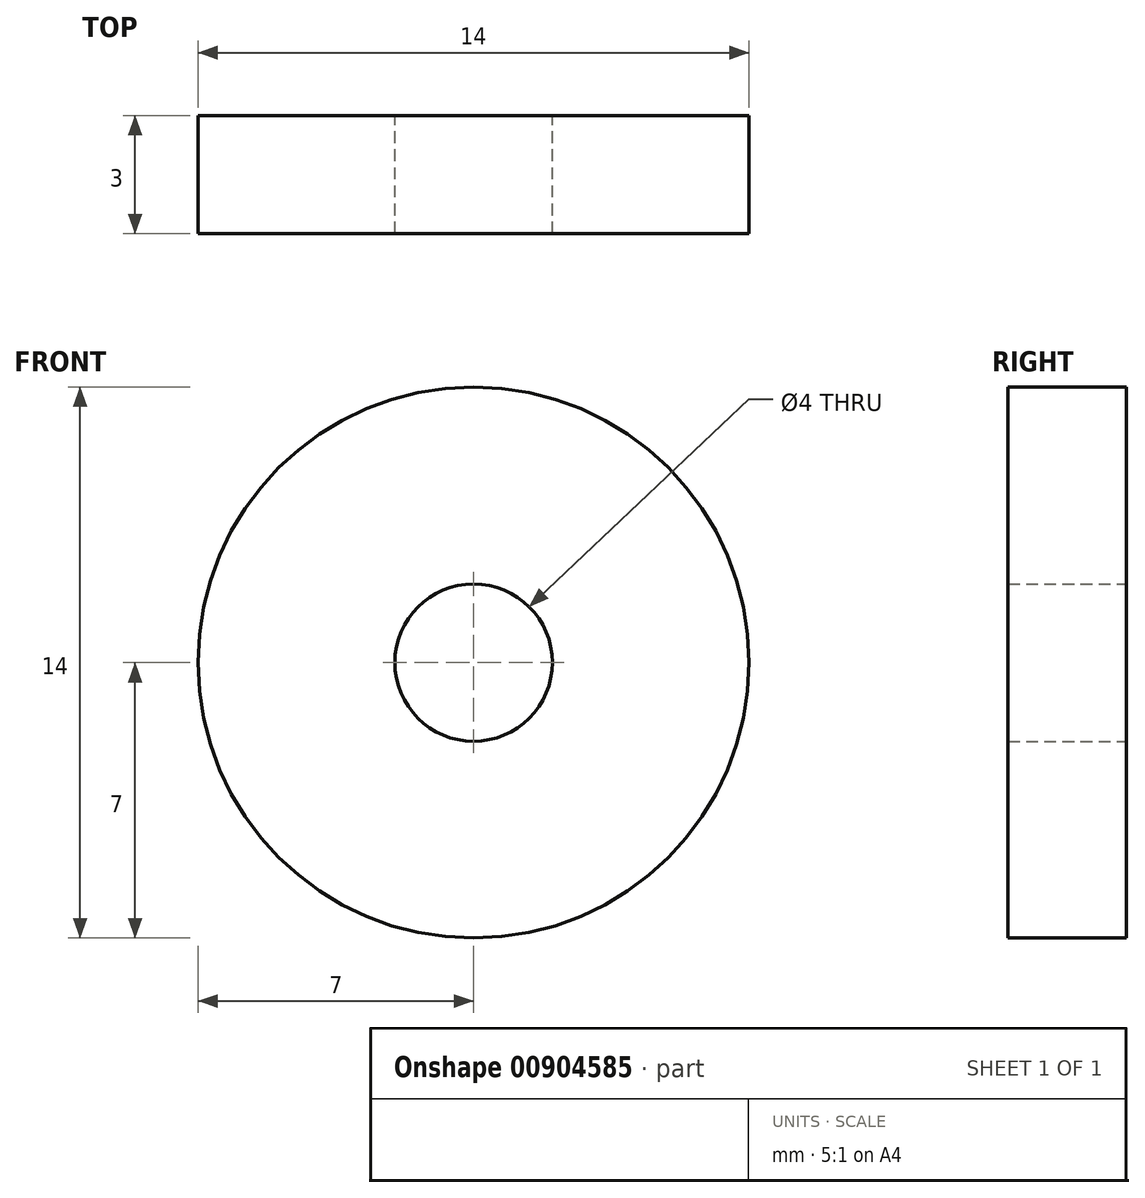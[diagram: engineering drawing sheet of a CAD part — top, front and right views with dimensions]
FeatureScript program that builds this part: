
annotation { "Feature Type Name" : "Feature", "Feature Type Description" : "" }
export const myFeature = defineFeature(function(context is Context, id is Id, definition is map)
    precondition{}
    {
        {
            var Q0;
            Q0=qCreatedBy(makeId("Front.planeOp"),FACE);
            var sketch = newSketch(context, id + "F0", { "sketchPlane" : qUnion([Q0])});
            skCircle(sketch, "E0", {"center": v(0, 0) * mm, "radius": 7 * mm});
            skCircle(sketch, "E1", {"center": v(0, 0) * mm, "radius": 2 * mm});
            skSolve(sketch);
        }
        {
            var Q0;
            Q0 = qSketchRegion(id + "F0", true);
            extrude(context, id + "F1", {"entities" : qUnion([Q0]), "depth" : 3 * mm, "offsetDistance" : 25 * mm});
        }
    });
